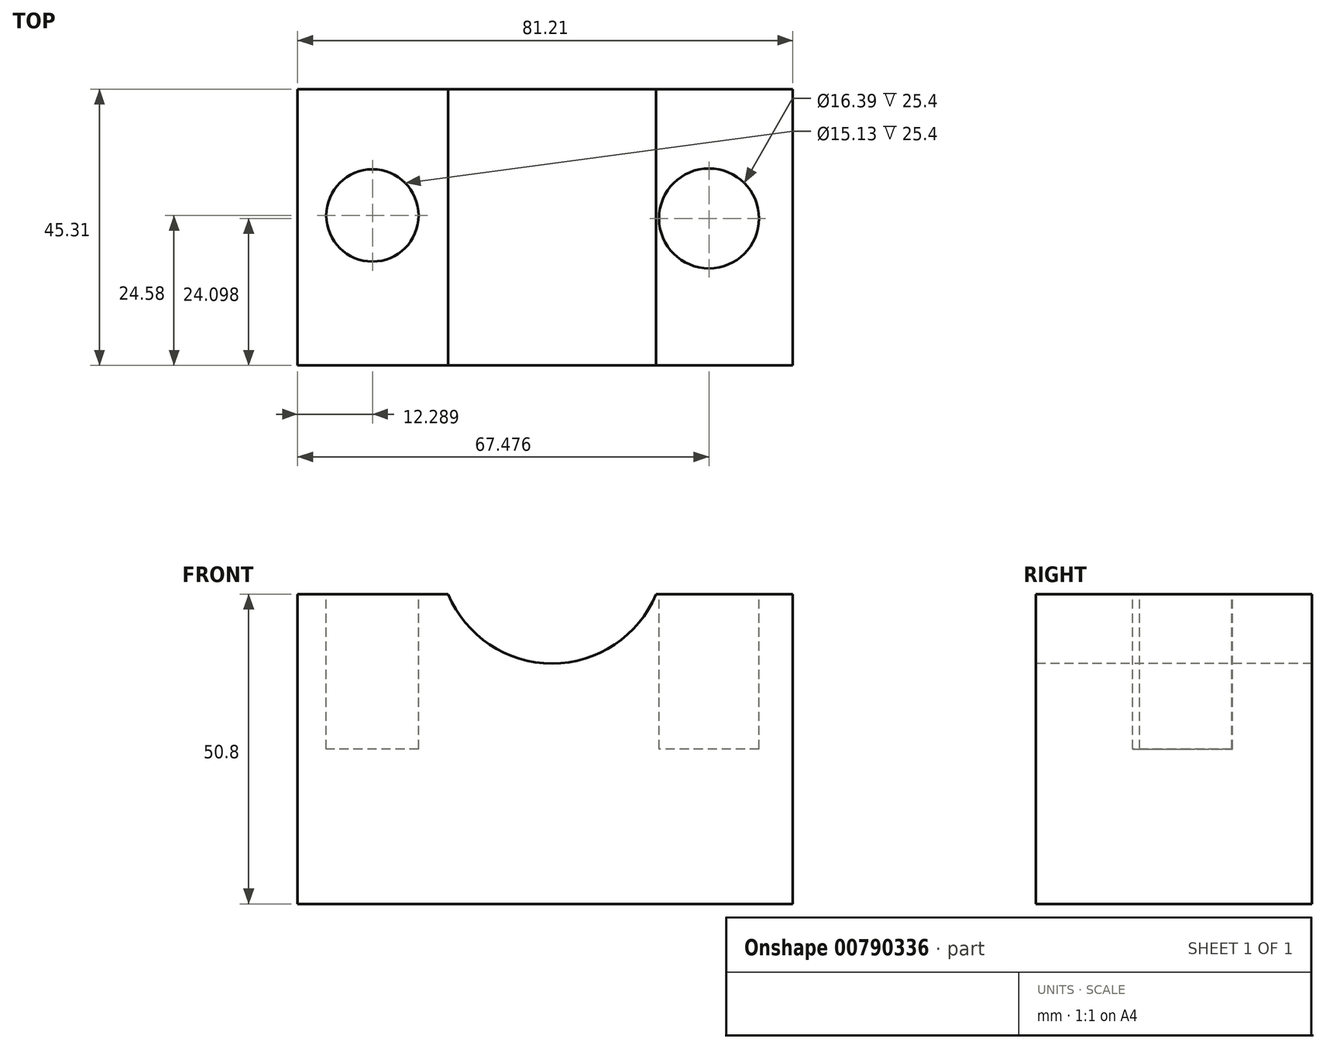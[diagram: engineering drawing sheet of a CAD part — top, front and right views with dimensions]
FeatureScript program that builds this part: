
annotation { "Feature Type Name" : "Feature", "Feature Type Description" : "" }
export const myFeature = defineFeature(function(context is Context, id is Id, definition is map)
    precondition{}
    {
        {
            var Q0;
            Q0=qCreatedBy(makeId("Top.planeOp"),FACE);
            var sketch = newSketch(context, id + "F0", { "sketchPlane" : qUnion([Q0])});
            skLineSegment(sketch, "E0.bottom", {"start": v(-24.7, 25.67) * mm, "end": v(56.51, 25.67) * mm});
            skLineSegment(sketch, "E0.top", {"start": v(-24.7, -19.64) * mm, "end": v(56.51, -19.64) * mm});
            skLineSegment(sketch, "E0.left", {"start": v(-24.7, 25.67) * mm, "end": v(-24.7, -19.64) * mm});
            skLineSegment(sketch, "E0.right", {"start": v(56.51, 25.67) * mm, "end": v(56.51, -19.64) * mm});
            skSolve(sketch);
        }
        {
            var Q0;
            Q0=makeQuery(id+"F0.imprint","IMPRINT",FACE,{"disambiguationData":[TD([[makeQuery(id+"F0.imprint","IMPRINT",EDGE,{"derivedFrom":sQuery(id+"F0.wireOp",EDGE,"E0.bottom")}),-1.0]])]});
            extrude(context, id + "F1", {"entities" : qUnion([Q0]), "depth" : 50.8 * mm, "offsetDistance" : 25.4 * mm});
        }
        {
            var Q0;
            Q0=makeQuery(id+"F1.opExtrude","CAP_FACE",FACE,{"disambiguationData":[OSD([sQuery(id+"F0.wireOp",EDGE,"E0.bottom"),sQuery(id+"F0.wireOp",EDGE,"E0.top"),sQuery(id+"F0.wireOp",EDGE,"E0.left"),sQuery(id+"F0.wireOp",EDGE,"E0.right")])],"isStart":false});
            var sketch = newSketch(context, id + "F2", { "sketchPlane" : qUnion([Q0])});
            skCircle(sketch, "E1", {"center": v(-12.41, 4.94) * mm, "radius": 7.57 * mm});
            skCircle(sketch, "E2", {"center": v(42.78, 4.46) * mm, "radius": 8.2 * mm});
            skSolve(sketch);
        }
        {
            var Q0;
            Q0=makeQuery(id+"F2.imprint","IMPRINT",FACE,{"disambiguationData":[TD([[makeQuery(id+"F2.imprint","IMPRINT",EDGE,{"derivedFrom":sQuery(id+"F2.wireOp",EDGE,"E1")}),1.0]])]});
            var Q1;
            Q1=makeQuery(id+"F2.imprint","IMPRINT",FACE,{"disambiguationData":[TD([[makeQuery(id+"F2.imprint","IMPRINT",EDGE,{"derivedFrom":sQuery(id+"F2.wireOp",EDGE,"E2")}),1.0]])]});
            extrude(context, id + "F3", {"entities" : qUnion([Q0, Q1]), "operationType" : NewBodyOperationType.REMOVE, "oppositeDirection" : true, "depth" : 25.4 * mm, "offsetDistance" : 25.4 * mm});
        }
        {
            var Q0;
            Q0=makeQuery(id+"F1.opExtrude","SWEPT_FACE",FACE,{"disambiguationData":[OSD([sQuery(id+"F0.wireOp",EDGE,"E0.top")])]});
            var sketch = newSketch(context, id + "F4", { "sketchPlane" : qUnion([Q0])});
            skArc(sketch, "E3", {"start": v(0, 50.8) * mm, "mid": v(17.05, 39.4) * mm, "end": v(34.1, 50.8) * mm});
            skSolve(sketch);
        }
        {
            var Q0;
            {var subQ0=sQuery(id+"F4.wireOp",EDGE,"E3");Q0=makeQuery(id+"F4.imprint","IMPRINT",FACE,{"disambiguationData":[TD([[makeQuery(id+"F4.imprint","IMPRINT",EDGE,{"derivedFrom":subQ0}),1.0]])]});}
            extrude(context, id + "F5", {"entities" : qUnion([Q0]), "operationType" : NewBodyOperationType.REMOVE, "oppositeDirection" : true, "depth" : 25.4 * mm, "offsetDistance" : 25.4 * mm});
        }
        {
            var Q0;
            Q0=makeQuery(id+"F5.boolean.opBoolean","COPY",FACE,{"derivedFrom":makeQuery(id+"F5.opExtrude","CAP_FACE",FACE,{"disambiguationData":[OSD([sQuery(id+"F0.wireOp",EDGE,"E0.top"),sQuery(id+"F4.wireOp",EDGE,"E3")])],"isStart":false})});
            var sketch = newSketch(context, id + "F6", { "sketchPlane" : qUnion([Q0])});
            skSolve(sketch);
        }
        {
            var Q0;
            Q0=makeQuery(id+"F6.imprint","IMPRINT",FACE,{"disambiguationData":[TD([[makeQuery(id+"F6.imprint","IMPRINT",EDGE,{"derivedFrom":makeQuery(id+"F5.boolean.opBoolean","COPY",EDGE,{"derivedFrom":makeQuery(id+"F5.opExtrude","CAP_EDGE",EDGE,{"disambiguationData":[OSD([sQuery(id+"F4.wireOp",EDGE,"E3")])],"isStart":false})})}),1.0]])]});
            extrude(context, id + "F7", {"entities" : qUnion([Q0]), "operationType" : NewBodyOperationType.REMOVE, "oppositeDirection" : true, "depth" : 25.4 * mm, "offsetDistance" : 25.4 * mm});
        }
    });
